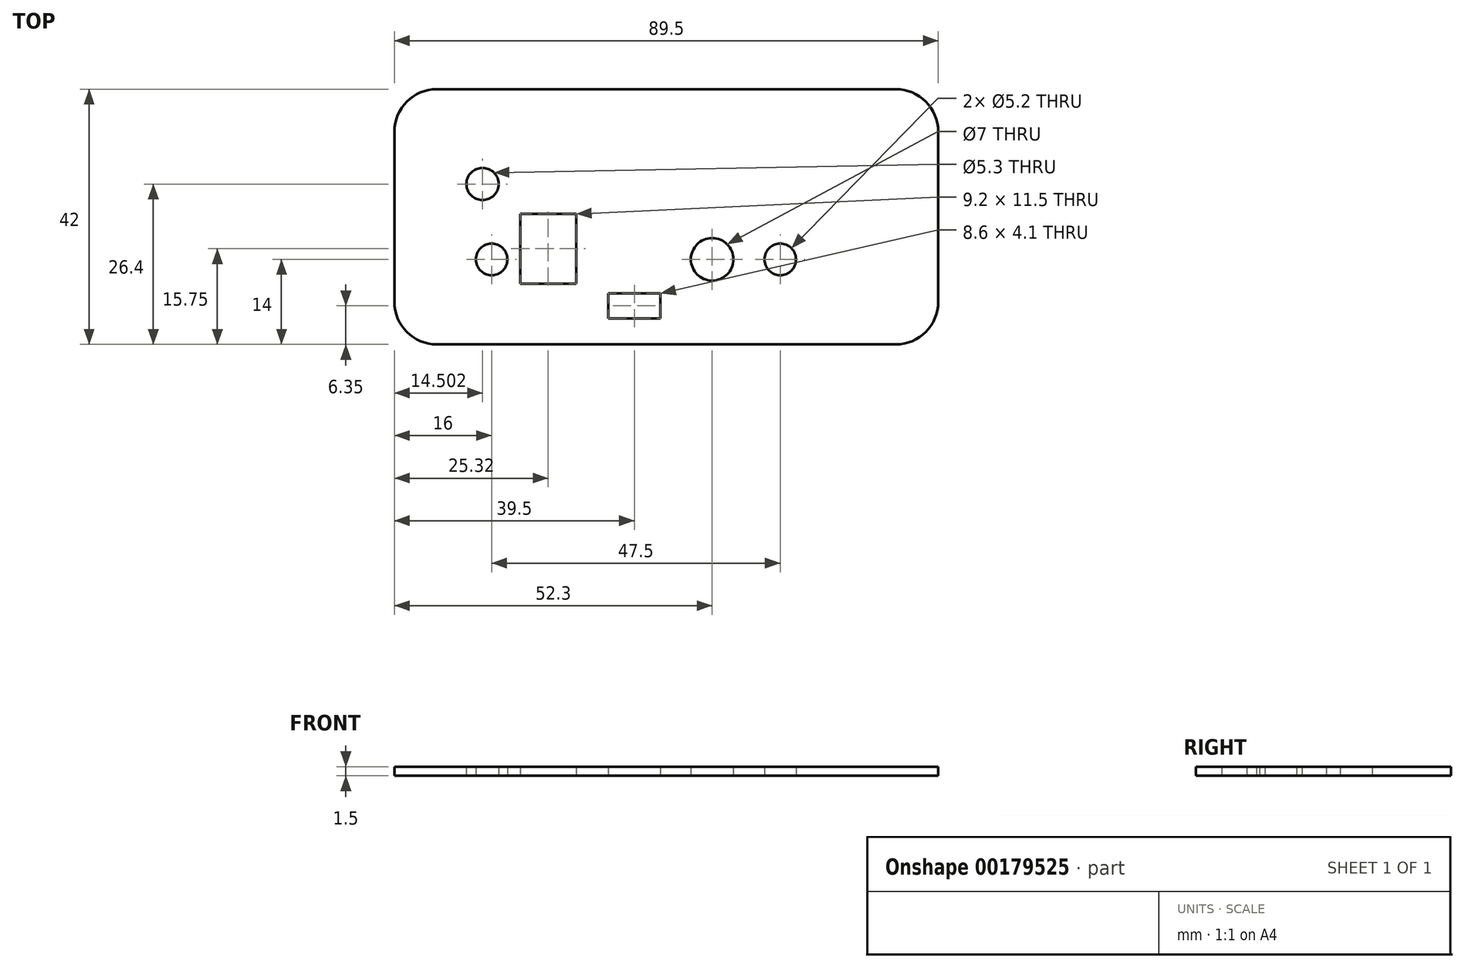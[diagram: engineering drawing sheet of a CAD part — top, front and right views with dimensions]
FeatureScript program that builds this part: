
annotation { "Feature Type Name" : "Feature", "Feature Type Description" : "" }
export const myFeature = defineFeature(function(context is Context, id is Id, definition is map)
    precondition{}
    {
        {
            var Q0;
            Q0=qCreatedBy(makeId("Top.planeOp"),FACE);
            var sketch = newSketch(context, id + "F0", { "sketchPlane" : qUnion([Q0])});
            skLineSegment(sketch, "E0.bottom", {"start": v(37.75, -21) * mm, "end": v(-37.75, -21) * mm});
            skLineSegment(sketch, "E0.top", {"start": v(37.75, 21) * mm, "end": v(-37.75, 21) * mm});
            skLineSegment(sketch, "E0.left", {"start": v(44.75, -14) * mm, "end": v(44.75, 14) * mm});
            skLineSegment(sketch, "E0.right", {"start": v(-44.75, -14) * mm, "end": v(-44.75, 14) * mm});
            skPoint(sketch, "E0.middle", {"position": v(0, 0) * mm});
            skPoint(sketch, "E1.visualSharp", {"position": v(-44.75, 21) * mm});
            skArc(sketch, "E1.filletArc", {"start": v(-37.75, 21) * mm, "mid": v(-42.7, 18.95) * mm, "end": v(-44.75, 14) * mm});
            skPoint(sketch, "E2.visualSharp", {"position": v(-44.75, -21) * mm});
            skArc(sketch, "E2.filletArc", {"start": v(-44.75, -14) * mm, "mid": v(-42.7, -18.95) * mm, "end": v(-37.75, -21) * mm});
            skPoint(sketch, "E3.visualSharp", {"position": v(44.75, 21) * mm});
            skArc(sketch, "E3.filletArc", {"start": v(44.75, 14) * mm, "mid": v(42.7, 18.95) * mm, "end": v(37.75, 21) * mm});
            skPoint(sketch, "E4.visualSharp", {"position": v(44.75, -21) * mm});
            skArc(sketch, "E4.filletArc", {"start": v(37.75, -21) * mm, "mid": v(42.7, -18.95) * mm, "end": v(44.75, -14) * mm});
            skLineSegment(sketch, "E5.bottom", {"start": v(-9.55, -12.6) * mm, "end": v(-0.95, -12.6) * mm});
            skLineSegment(sketch, "E5.top", {"start": v(-9.55, -16.7) * mm, "end": v(-0.95, -16.7) * mm});
            skLineSegment(sketch, "E5.left", {"start": v(-9.55, -12.6) * mm, "end": v(-9.55, -16.7) * mm});
            skLineSegment(sketch, "E5.right", {"start": v(-0.95, -12.6) * mm, "end": v(-0.95, -16.7) * mm});
            skPoint(sketch, "E6", {"position": v(7.55, -7) * mm});
            skPoint(sketch, "E7", {"position": v(18.75, -7) * mm});
            skPoint(sketch, "E8", {"position": v(-28.75, -7) * mm});
            skLineSegment(sketch, "E9.bottom", {"start": v(-24.03, 0.5) * mm, "end": v(-14.83, 0.5) * mm});
            skLineSegment(sketch, "E9.top", {"start": v(-24.03, -11) * mm, "end": v(-14.83, -11) * mm});
            skLineSegment(sketch, "E9.left", {"start": v(-24.03, 0.5) * mm, "end": v(-24.03, -11) * mm});
            skLineSegment(sketch, "E9.right", {"start": v(-14.83, 0.5) * mm, "end": v(-14.83, -11) * mm});
            skPoint(sketch, "E10", {"position": v(-30.25, 5.4) * mm});
            skLineSegment(sketch, "E11.direction1", {"start": v(-30.25, 5.4) * mm, "end": v(-22, 5.4) * mm, "construction": true});
            skLineSegment(sketch, "E11.direction2", {"start": v(-30.25, 5.4) * mm, "end": v(-30.25, 15.4) * mm, "construction": true});
            skSolve(sketch);
        }
        {
            var Q0;
            Q0=makeQuery(id+"F0.imprint","IMPRINT",FACE,{"disambiguationData":[TD([[makeQuery(id+"F0.imprint","IMPRINT",EDGE,{"derivedFrom":sQuery(id+"F0.wireOp",EDGE,"E0.bottom")}),-1.0]])]});
            extrude(context, id + "F1", {"entities" : qUnion([Q0]), "depth" : 1.5 * mm});
        }
        {
            var Q0;
            Q0=sQuery(id+"F0.wireOp",VERTEX,"E7");
            var Q1;
            Q1=sQuery(id+"F0.wireOp",VERTEX,"E8");
            var Q2;
            Q2=makeQuery(id+"F1.opExtrude","SWEPT_BODY",BODY,{"disambiguationData":[OSD([sQuery(id+"F0.wireOp",EDGE,"E0.bottom"),sQuery(id+"F0.wireOp",EDGE,"E0.top"),sQuery(id+"F0.wireOp",EDGE,"E0.left"),sQuery(id+"F0.wireOp",EDGE,"E0.right"),sQuery(id+"F0.wireOp",EDGE,"E1.filletArc"),sQuery(id+"F0.wireOp",EDGE,"E2.filletArc"),sQuery(id+"F0.wireOp",EDGE,"E3.filletArc"),sQuery(id+"F0.wireOp",EDGE,"E4.filletArc"),sQuery(id+"F0.wireOp",EDGE,"E5.bottom"),sQuery(id+"F0.wireOp",EDGE,"E5.top"),sQuery(id+"F0.wireOp",EDGE,"E5.left"),sQuery(id+"F0.wireOp",EDGE,"E5.right"),sQuery(id+"F0.wireOp",EDGE,"E9.bottom"),sQuery(id+"F0.wireOp",EDGE,"E9.top"),sQuery(id+"F0.wireOp",EDGE,"E9.left"),sQuery(id+"F0.wireOp",EDGE,"E9.right")])]});
            hole(context, id + "F2", {"style" : HoleStyle.SIMPLE, "endStyle" : HoleEndStyle.BLIND, "oppositeDirection" : true, "holeDiameter" : 5.2 * mm, "holeDepth" : 2 * mm, "locations" : qUnion([Q0, Q1]), "scope" : qUnion([Q2])});
        }
        {
            var Q0;
            Q0=sQuery(id+"F0.wireOp",VERTEX,"E6");
            var Q1;
            Q1=makeQuery(id+"F1.opExtrude","SWEPT_BODY",BODY,{"disambiguationData":[OSD([sQuery(id+"F0.wireOp",EDGE,"E0.bottom"),sQuery(id+"F0.wireOp",EDGE,"E0.top"),sQuery(id+"F0.wireOp",EDGE,"E0.left"),sQuery(id+"F0.wireOp",EDGE,"E0.right"),sQuery(id+"F0.wireOp",EDGE,"E1.filletArc"),sQuery(id+"F0.wireOp",EDGE,"E2.filletArc"),sQuery(id+"F0.wireOp",EDGE,"E3.filletArc"),sQuery(id+"F0.wireOp",EDGE,"E4.filletArc"),sQuery(id+"F0.wireOp",EDGE,"E5.bottom"),sQuery(id+"F0.wireOp",EDGE,"E5.top"),sQuery(id+"F0.wireOp",EDGE,"E5.left"),sQuery(id+"F0.wireOp",EDGE,"E5.right"),sQuery(id+"F0.wireOp",EDGE,"E9.bottom"),sQuery(id+"F0.wireOp",EDGE,"E9.top"),sQuery(id+"F0.wireOp",EDGE,"E9.left"),sQuery(id+"F0.wireOp",EDGE,"E9.right")])]});
            hole(context, id + "F3", {"style" : HoleStyle.SIMPLE, "endStyle" : HoleEndStyle.BLIND, "oppositeDirection" : true, "holeDiameter" : 7 * mm, "holeDepth" : 2 * mm, "locations" : qUnion([Q0]), "scope" : qUnion([Q1])});
        }
        {
            var Q0;
            Q0=sQuery(id+"F0.wireOp",VERTEX,"E10");
            var Q1;
            Q1=sQuery(id+"F0.wireOp",VERTEX,"E11.0.1.0");
            var Q2;
            Q2=sQuery(id+"F0.wireOp",VERTEX,"E11.1.1.0");
            var Q3;
            Q3=sQuery(id+"F0.wireOp",VERTEX,"E11.1.0.0");
            var Q4;
            Q4=sQuery(id+"F0.wireOp",VERTEX,"E11.2.1.0");
            var Q5;
            Q5=sQuery(id+"F0.wireOp",VERTEX,"E11.2.0.0");
            var Q6;
            Q6=sQuery(id+"F0.wireOp",VERTEX,"E11.3.1.0");
            var Q7;
            Q7=sQuery(id+"F0.wireOp",VERTEX,"E11.3.0.0");
            var Q8;
            Q8=sQuery(id+"F0.wireOp",VERTEX,"E11.4.1.0");
            var Q9;
            Q9=sQuery(id+"F0.wireOp",VERTEX,"E11.4.0.0");
            var Q10;
            Q10=sQuery(id+"F0.wireOp",VERTEX,"E11.5.1.0");
            var Q11;
            Q11=sQuery(id+"F0.wireOp",VERTEX,"E11.5.0.0");
            var Q12;
            Q12=sQuery(id+"F0.wireOp",VERTEX,"E11.6.1.0");
            var Q13;
            Q13=sQuery(id+"F0.wireOp",VERTEX,"E11.6.0.0");
            var Q14;
            Q14=makeQuery(id+"F1.opExtrude","SWEPT_BODY",BODY,{"disambiguationData":[OSD([sQuery(id+"F0.wireOp",EDGE,"E0.bottom"),sQuery(id+"F0.wireOp",EDGE,"E0.top"),sQuery(id+"F0.wireOp",EDGE,"E0.left"),sQuery(id+"F0.wireOp",EDGE,"E0.right"),sQuery(id+"F0.wireOp",EDGE,"E1.filletArc"),sQuery(id+"F0.wireOp",EDGE,"E2.filletArc"),sQuery(id+"F0.wireOp",EDGE,"E3.filletArc"),sQuery(id+"F0.wireOp",EDGE,"E4.filletArc"),sQuery(id+"F0.wireOp",EDGE,"E5.bottom"),sQuery(id+"F0.wireOp",EDGE,"E5.top"),sQuery(id+"F0.wireOp",EDGE,"E5.left"),sQuery(id+"F0.wireOp",EDGE,"E5.right"),sQuery(id+"F0.wireOp",EDGE,"E9.bottom"),sQuery(id+"F0.wireOp",EDGE,"E9.top"),sQuery(id+"F0.wireOp",EDGE,"E9.left"),sQuery(id+"F0.wireOp",EDGE,"E9.right")])]});
            hole(context, id + "F4", {"style" : HoleStyle.SIMPLE, "endStyle" : HoleEndStyle.BLIND, "oppositeDirection" : true, "holeDiameter" : 5.3 * mm, "holeDepth" : 2 * mm, "locations" : qUnion([Q0, Q1, Q2, Q3, Q4, Q5, Q6, Q7, Q8, Q9, Q10, Q11, Q12, Q13]), "scope" : qUnion([Q14])});
        }
    });
